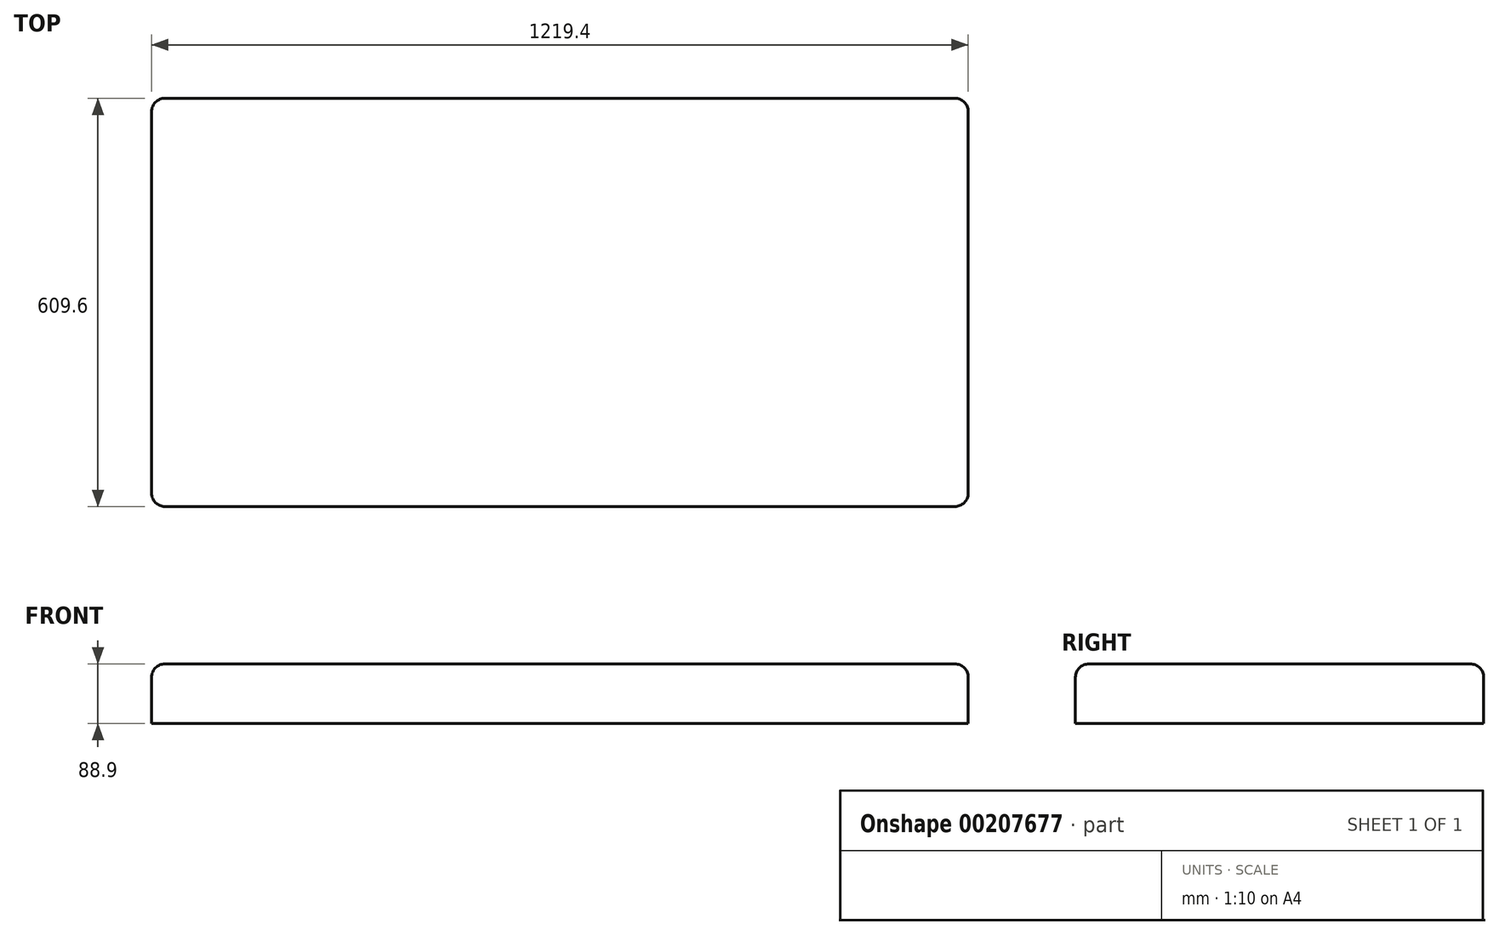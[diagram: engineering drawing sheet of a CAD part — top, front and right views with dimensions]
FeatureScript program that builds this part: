
annotation { "Feature Type Name" : "Feature", "Feature Type Description" : "" }
export const myFeature = defineFeature(function(context is Context, id is Id, definition is map)
    precondition{}
    {
        {
            var Q0;
            Q0=qCreatedBy(makeId("Top.planeOp"),FACE);
            var sketch = newSketch(context, id + "F0", { "sketchPlane" : qUnion([Q0])});
            skLineSegment(sketch, "E0.bottom", {"start": v(-609.7, 304.8) * mm, "end": v(609.7, 304.8) * mm});
            skLineSegment(sketch, "E0.top", {"start": v(-609.7, -304.8) * mm, "end": v(609.7, -304.8) * mm});
            skLineSegment(sketch, "E0.left", {"start": v(-609.7, 304.8) * mm, "end": v(-609.7, -304.8) * mm});
            skLineSegment(sketch, "E0.right", {"start": v(609.7, 304.8) * mm, "end": v(609.7, -304.8) * mm});
            skPoint(sketch, "E0.middle", {"position": v(0, 0) * mm});
            skSolve(sketch);
        }
        {
            var Q0;
            Q0 = qSketchRegion(id + "F0", true);
            extrude(context, id + "F1", {"entities" : qUnion([Q0]), "depth" : 88.9 * mm});
        }
        {
            var Q0;
            Q0=makeQuery(id+"F1.opExtrude","CAP_EDGE",EDGE,{"disambiguationData":[OSD([sQuery(id+"F0.wireOp",EDGE,"E0.bottom")])],"isStart":false});
            var Q1;
            Q1=makeQuery(id+"F1.opExtrude","CAP_EDGE",EDGE,{"disambiguationData":[OSD([sQuery(id+"F0.wireOp",EDGE,"E0.left")])],"isStart":false});
            var Q2;
            Q2=makeQuery(id+"F1.opExtrude","CAP_EDGE",EDGE,{"disambiguationData":[OSD([sQuery(id+"F0.wireOp",EDGE,"E0.top")])],"isStart":false});
            var Q3;
            Q3=makeQuery(id+"F1.opExtrude","CAP_EDGE",EDGE,{"disambiguationData":[OSD([sQuery(id+"F0.wireOp",EDGE,"E0.right")])],"isStart":false});
            var Q4;
            Q4=makeQuery(id+"F1.opExtrude","SWEPT_EDGE",EDGE,{"disambiguationData":[OSD([sQuery(id+"F0.wireOp",EDGE,"E0.top"),sQuery(id+"F0.wireOp",EDGE,"E0.left")])]});
            var Q5;
            Q5=makeQuery(id+"F1.opExtrude","SWEPT_EDGE",EDGE,{"disambiguationData":[OSD([sQuery(id+"F0.wireOp",EDGE,"E0.top"),sQuery(id+"F0.wireOp",EDGE,"E0.right")])]});
            var Q6;
            Q6=makeQuery(id+"F1.opExtrude","SWEPT_EDGE",EDGE,{"disambiguationData":[OSD([sQuery(id+"F0.wireOp",EDGE,"E0.bottom"),sQuery(id+"F0.wireOp",EDGE,"E0.right")])]});
            var Q7;
            Q7=makeQuery(id+"F1.opExtrude","SWEPT_EDGE",EDGE,{"disambiguationData":[OSD([sQuery(id+"F0.wireOp",EDGE,"E0.bottom"),sQuery(id+"F0.wireOp",EDGE,"E0.left")])]});
            fillet(context, id + "F2", {"entities" : qUnion([Q0, Q1, Q2, Q3, Q4, Q5, Q6, Q7]), "radius" : 20 * mm, "tangentPropagation" : true, "allowEdgeOverflow" : false});
        }
    });
